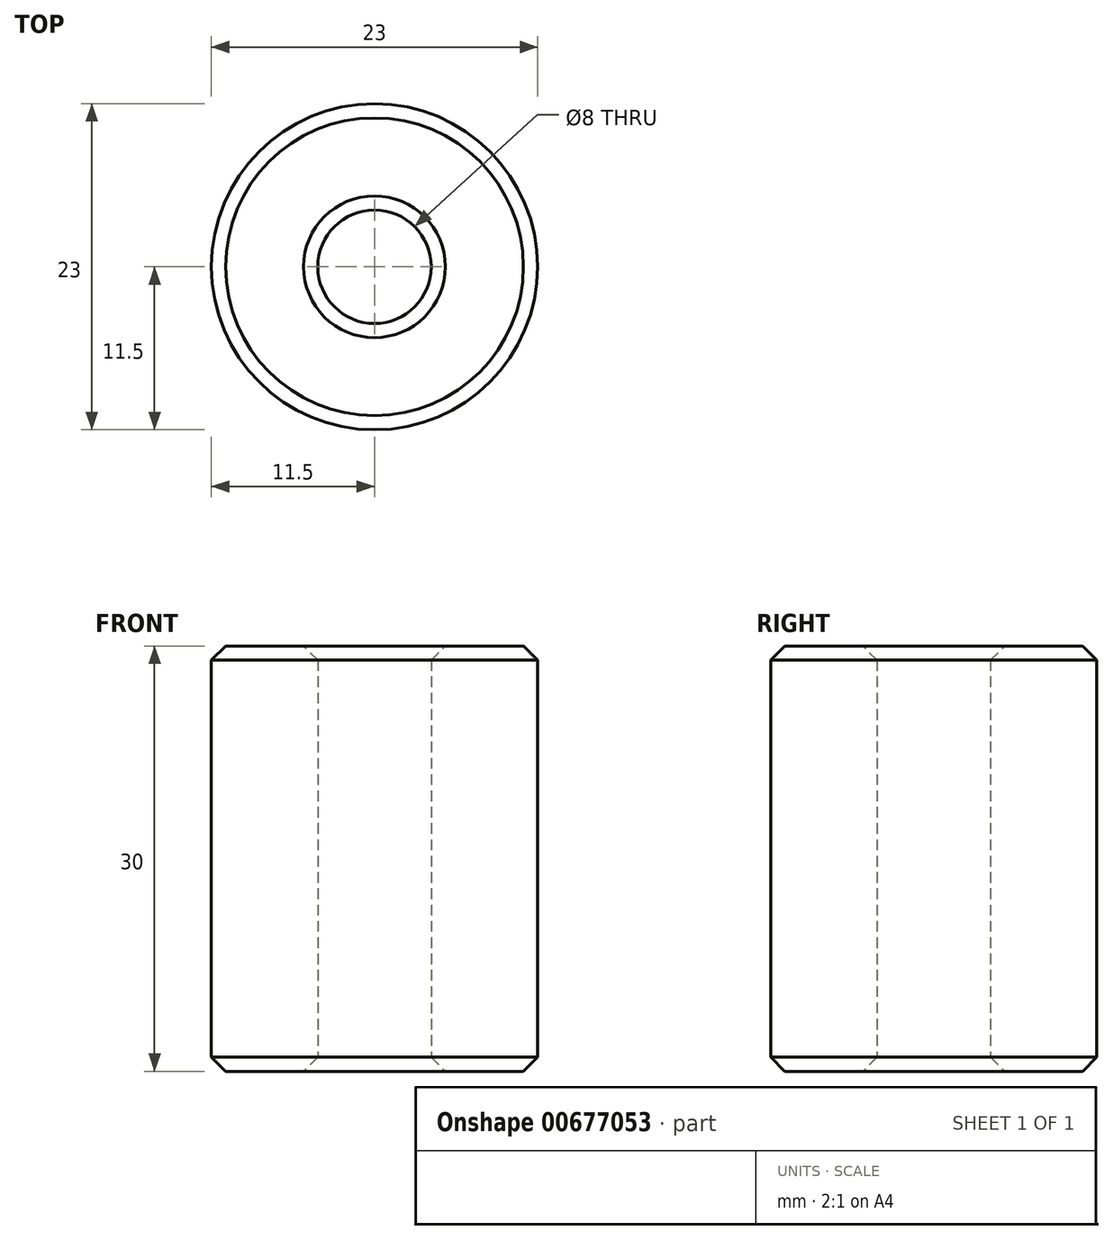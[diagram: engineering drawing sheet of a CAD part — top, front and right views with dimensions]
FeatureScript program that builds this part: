
annotation { "Feature Type Name" : "Feature", "Feature Type Description" : "" }
export const myFeature = defineFeature(function(context is Context, id is Id, definition is map)
    precondition{}
    {
        {
            var Q0;
            Q0=qCreatedBy(makeId("Top.planeOp"),FACE);
            var sketch = newSketch(context, id + "F0", { "sketchPlane" : qUnion([Q0])});
            skCircle(sketch, "E0", {"center": v(0, 0) * mm, "radius": 4 * mm});
            skCircle(sketch, "E1", {"center": v(0, 0) * mm, "radius": 11.5 * mm});
            skSolve(sketch);
        }
        {
            var Q0;
            Q0 = qSketchRegion(id + "F0", true);
            extrude(context, id + "F1", {"entities" : qUnion([Q0]), "depth" : 30 * mm, "offsetDistance" : 25 * mm});
        }
        {
            var Q0;
            Q0=makeQuery(id+"F1.opExtrude","CAP_EDGE",EDGE,{"disambiguationData":[OSD([sQuery(id+"F0.wireOp",EDGE,"E0")])],"isStart":false});
            var Q1;
            Q1=makeQuery(id+"F1.opExtrude","CAP_EDGE",EDGE,{"disambiguationData":[OSD([sQuery(id+"F0.wireOp",EDGE,"E1")])],"isStart":false});
            var Q2;
            Q2=makeQuery(id+"F1.opExtrude","CAP_EDGE",EDGE,{"disambiguationData":[OSD([sQuery(id+"F0.wireOp",EDGE,"E0")])],"isStart":true});
            var Q3;
            Q3=makeQuery(id+"F1.opExtrude","SWEPT_FACE",FACE,{"disambiguationData":[OSD([sQuery(id+"F0.wireOp",EDGE,"E1")])]});
            chamfer(context, id + "F2", {"entities" : qUnion([Q0, Q1, Q2, Q3]), "width" : 1 * mm, "tangentPropagation" : true});
        }
    });
